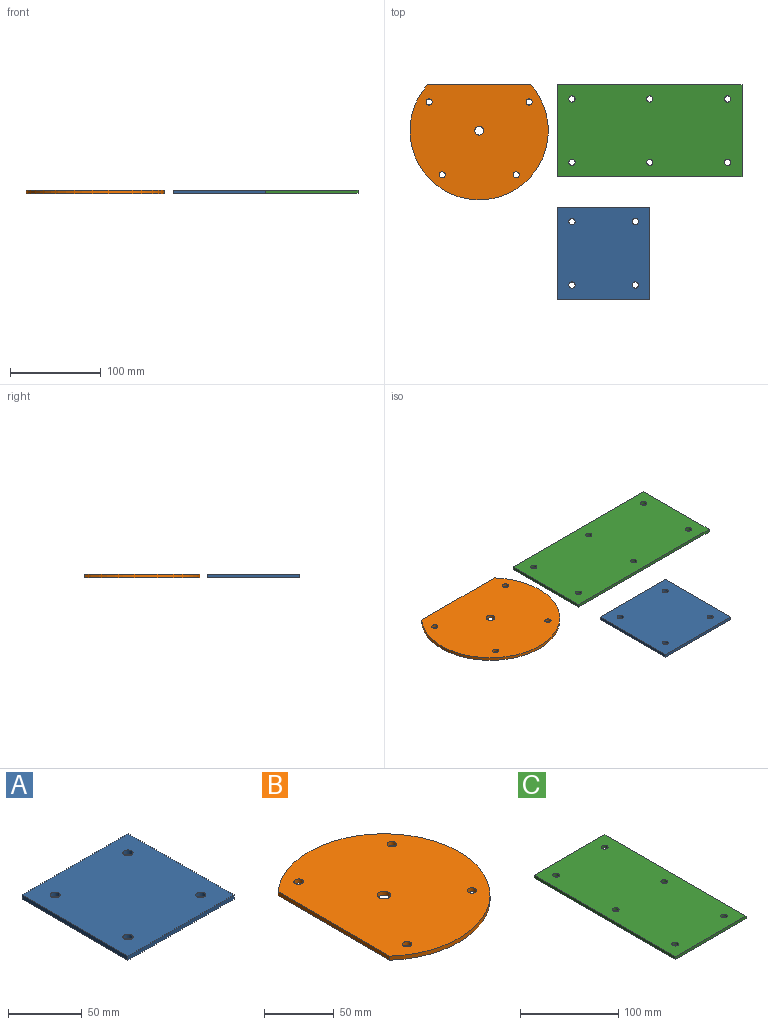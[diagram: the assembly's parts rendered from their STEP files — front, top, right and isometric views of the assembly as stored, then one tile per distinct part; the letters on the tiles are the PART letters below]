
ASSEMBLY  parts=3 mates=4
PART A: 10 faces, bbox 101.6x101.6x3.4 mm
  f0: plane 101.6x101.6mm, normal (0,0,1), area 10174.8mm2, adj f2,f3,f4,f5,f6,f7,f8,f9
  f1: plane 101.6x101.6mm, normal (0,0,-1), area 10174.8mm2, adj f2,f3,f4,f5,f6,f7,f8,f9
  f2: plane 101.6x3.43mm, normal (-1,0,0), area 348.4mm2, adj f0,f1,f3,f5
  f3: plane 101.6x3.43mm, normal (0,-1,0), area 348.4mm2, adj f0,f1,f2,f4
  f4: plane 101.6x3.43mm, normal (1,0,0), area 348.4mm2, adj f0,f1,f3,f5
  f5: plane 101.6x3.43mm, normal (0,1,0), area 348.4mm2, adj f0,f1,f2,f4
  f6: cylinder r=3.43mm len=6.86mm, axis (0,0,-1), area 73.9mm2, adj f0,f1
  f7: cylinder r=3.43mm len=6.86mm, axis (0,0,-1), area 73.9mm2, adj f0,f1
  f8: cylinder r=3.43mm len=6.86mm, axis (0,0,-1), area 73.9mm2, adj f0,f1
  f9: cylinder r=3.43mm len=6.86mm, axis (0,0,-1), area 73.9mm2, adj f0,f1
PART B: 9 faces, bbox 127x152.4x3.6 mm
  f0: plane 152.4x127mm, normal (0,0,1), area 16026.5mm2, adj f2,f3,f4,f5,f6,f7,f8
  f1: plane 152.4x127mm, normal (0,0,-1), area 16026.5mm2, adj f2,f3,f4,f5,f6,f7,f8
  f2: cylinder r=76.2mm len=152.4mm, axis (0,0,-1), area 1246.7mm2, adj f0,f1,f4
  f3: cylinder r=4.83mm len=9.65mm, axis (0,0,-1), area 107.8mm2, adj f0,f1
  f4: plane 113.59x3.56mm, normal (-1,0,0), area 403.9mm2, adj f0,f1,f2
  f5: cylinder r=3.38mm len=6.76mm, axis (0,0,1), area 75.5mm2, adj f0,f1
  f6: cylinder r=3.38mm len=6.76mm, axis (0,0,1), area 75.5mm2, adj f0,f1
  f7: cylinder r=3.38mm len=6.76mm, axis (0,0,1), area 75.5mm2, adj f0,f1
  f8: cylinder r=3.38mm len=6.76mm, axis (0,0,1), area 75.5mm2, adj f0,f1
PART C: 12 faces, bbox 101.6x203.2x3.4 mm
  f0: plane 203.2x101.6mm, normal (0,0,1), area 20423.5mm2, adj f2,f3,f4,f5,f6,f7,f8,f9
  f1: plane 203.2x101.6mm, normal (0,0,-1), area 20423.5mm2, adj f2,f3,f4,f5,f6,f7,f8,f9
  f2: plane 203.2x3.43mm, normal (-1,0,0), area 696.8mm2, adj f0,f1,f3,f5
  f3: plane 101.6x3.43mm, normal (0,-1,0), area 348.4mm2, adj f0,f1,f2,f4
  f4: plane 203.2x3.43mm, normal (1,0,0), area 696.8mm2, adj f0,f1,f3,f5
  f5: plane 101.6x3.43mm, normal (0,1,0), area 348.4mm2, adj f0,f1,f2,f4
  f6: cylinder r=3.43mm len=6.86mm, axis (0,0,-1), area 73.9mm2, adj f0,f1
  f7: cylinder r=3.43mm len=6.86mm, axis (0,0,-1), area 73.9mm2, adj f0,f1
  f8: cylinder r=3.43mm len=6.86mm, axis (0,0,-1), area 73.9mm2, adj f0,f1
  f9: cylinder r=3.43mm len=6.86mm, axis (0,0,-1), area 73.9mm2, adj f0,f1
  f10: cylinder r=3.43mm len=6.86mm, axis (0,0,-1), area 73.9mm2, adj f0,f1
  f11: cylinder r=3.43mm len=6.86mm, axis (0,0,-1), area 73.9mm2, adj f0,f1
PLACE A t=(84.11,-236.68,-3.43)mm
PLACE B rot(axis=(0,0,-1),90deg) t=(-2.3,-50.8,-3.56)mm
PLACE C rot(axis=(0,0,-1),90deg) t=(84.11,0,-3.43)mm
MATE planar B.f4 <-> C.f2  axis (0,1,0) through (-2.3,0,-1.78)mm
MATE planar C.f3 <-> A.f2  axis (-1,0,0) through (84.11,-50.8,-1.71)mm
MATE planar B.f0 <-> C.f0  axis (0,0,1) through (-2.3,-58.34,0)mm
MATE planar A.f8 <-> C.f0  axis (0,0,1) through (99.98,-150.96,0)mm
